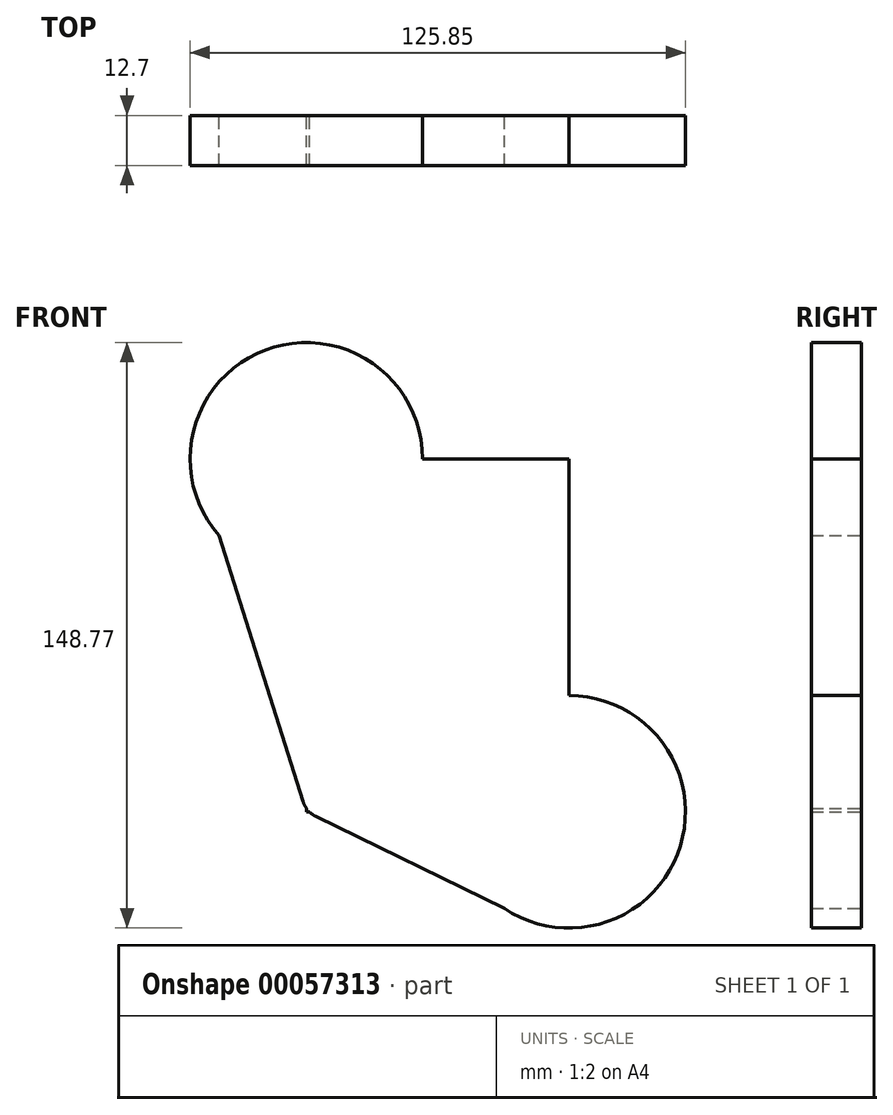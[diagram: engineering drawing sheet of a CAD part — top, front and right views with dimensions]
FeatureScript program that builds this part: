
annotation { "Feature Type Name" : "Feature", "Feature Type Description" : "" }
export const myFeature = defineFeature(function(context is Context, id is Id, definition is map)
    precondition{}
    {
        {
            var Q0;
            Q0=qCreatedBy(makeId("Front.planeOp"),FACE);
            var sketch = newSketch(context, id + "F0", { "sketchPlane" : qUnion([Q0])});
            skLineSegment(sketch, "E0.bottom", {"start": v(-30.67, 42.5) * mm, "end": v(36.1, 42.5) * mm});
            skLineSegment(sketch, "E0.top", {"start": v(-30.67, -47.2) * mm, "end": v(36.1, -47.2) * mm});
            skLineSegment(sketch, "E0.left", {"start": v(-30.67, 42.5) * mm, "end": v(-30.67, -47.2) * mm});
            skLineSegment(sketch, "E0.right", {"start": v(36.1, 42.5) * mm, "end": v(36.1, -47.2) * mm});
            skCircle(sketch, "E1", {"center": v(-30.67, 42.5) * mm, "radius": 29.53 * mm});
            skCircle(sketch, "E2", {"center": v(36.1, -47.2) * mm, "radius": 29.53 * mm});
            skLineSegment(sketch, "E3", {"start": v(-52.85, 23) * mm, "end": v(-31.5, -44.6) * mm});
            skLineSegment(sketch, "E4", {"start": v(-28.22, -48.4) * mm, "end": v(19.63, -71.7) * mm});
            skPoint(sketch, "E5.visualSharp", {"position": v(-30.67, -47.2) * mm});
            skArc(sketch, "E5.filletArc", {"start": v(-31.5, -44.6) * mm, "mid": v(-30.25, -46.83) * mm, "end": v(-28.22, -48.4) * mm});
            skSolve(sketch);
        }
        {
            var Q0;
            Q0 = qSketchRegion(id + "F0", true);
            extrude(context, id + "F1", {"entities" : qUnion([Q0]), "depth" : 12.7 * mm});
        }
    });
